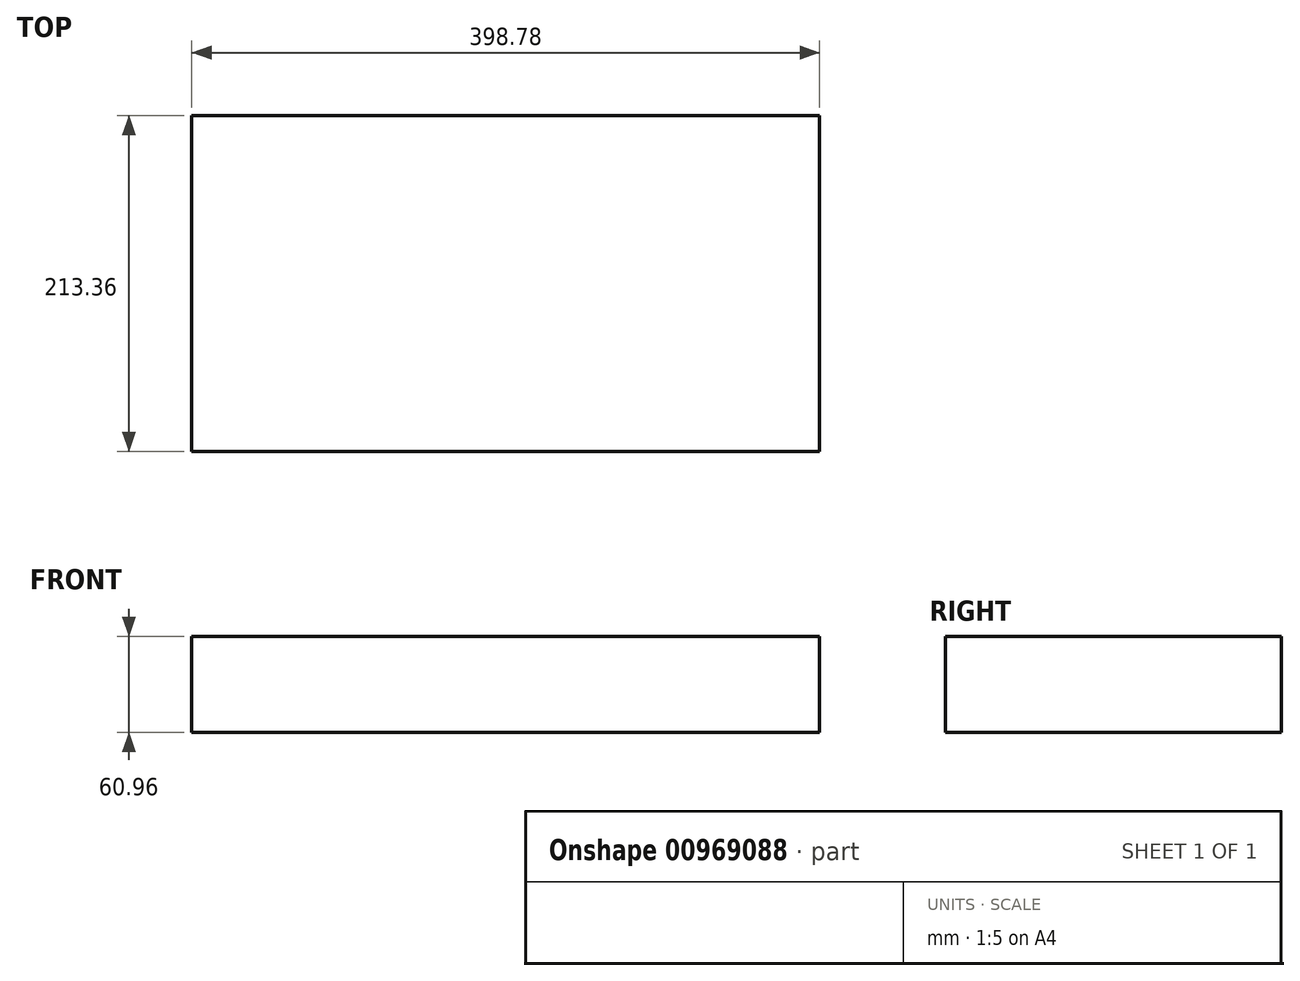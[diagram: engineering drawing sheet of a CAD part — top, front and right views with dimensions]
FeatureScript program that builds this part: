
annotation { "Feature Type Name" : "Feature", "Feature Type Description" : "" }
export const myFeature = defineFeature(function(context is Context, id is Id, definition is map)
    precondition{}
    {
        {
            var Q0;
            Q0=qCreatedBy(makeId("Top.planeOp"),FACE);
            var sketch = newSketch(context, id + "F0", { "sketchPlane" : qUnion([Q0])});
            skLineSegment(sketch, "E0.bottom", {"start": v(0, 0) * mm, "end": v(398.78, 0) * mm});
            skLineSegment(sketch, "E0.top", {"start": v(0, 213.36) * mm, "end": v(398.78, 213.36) * mm});
            skLineSegment(sketch, "E0.left", {"start": v(0, 0) * mm, "end": v(0, 213.36) * mm});
            skLineSegment(sketch, "E0.right", {"start": v(398.78, 0) * mm, "end": v(398.78, 213.36) * mm});
            skSolve(sketch);
        }
        {
            var Q0;
            Q0 = qSketchRegion(id + "F0", true);
            extrude(context, id + "F1", {"entities" : qUnion([Q0]), "depth" : 60.96 * mm, "offsetDistance" : 25.4 * mm});
        }
    });
